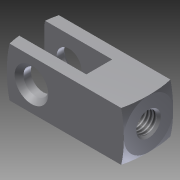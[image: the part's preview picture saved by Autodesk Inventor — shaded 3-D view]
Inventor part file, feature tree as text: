
AUTODESK INVENTOR PART (.ipt)
format: ipt  version: 2012 (Build 160160000, 160)  size: 180,224 bytes
history: native  units: in
note: dims shown in document units (in); Inventor stores cm internally (conversion verified against a paired STEP export)
features: other x126, sketch x7, revolve x3, extrude x2, hole x2
ambient origin geometry x8: Origin, YZ Plane, XZ Plane, XY Plane, X Axis, Y Axis, Z Axis, Center Point
bodies: Solid1 (feature_tree)
feature tree (140):
  extrude  "Extrusion1"  Depth=0.5in TaperAngle=0.0deg
  extrude  "Extrusion2"  TaperAngle=360.0deg  [1 undecoded]
  hole  "Drilling 1"  [1 undecoded]
  hole  "Drilling 2"  [1 undecoded]
  revolve  "Revolution1"  [1 undecoded]
  revolve  "Revolution2"  [1 undecoded]
  revolve  "Revolution3"  [1 undecoded]
  other  "th1_XY"
  other  "th1_YZ"
  other  "th1_ZX"
  other  "th1_X"
  other  "th1_Y"
  other  "th1_Z"
  other  "th1_Center"
  other  "th2_XY"
  other  "th2_YZ"
  other  "th2_ZX"
  other  "th2_X"
  other  "th2_Y"
  other  "th2_Z"
  other  "th2_Center"
  other  "rod_clevis_body_XY"
  other  "rod_clevis_body_YZ"
  other  "rod_clevis_body_ZX"
  other  "rod_clevis_body_X"
  other  "rod_clevis_body_Y"
  other  "rod_clevis_body_Z"
  other  "rod_clevis_body_Center"
  other  "piston_rod_clevis_XY"
  other  "piston_rod_clevis_YZ"
  other  "piston_rod_clevis_ZX"
  other  "piston_rod_clevis_X"
  other  "piston_rod_clevis_Y"
  other  "piston_rod_clevis_Z"
  other  "piston_rod_clevis_Center"
  other  "dummy_XY"
  other  "dummy_YZ"
  other  "dummy_ZX"
  other  "dummy_X"
  other  "dummy_Y"
  other  "dummy_Z"
  other  "dummy_Center"
  other  "l11_XY"
  other  "l11_YZ"
  other  "l11_ZX"
  other  "l11_X"
  other  "l11_Y"
  other  "l11_Z"
  other  "l11_Center"
  other  "l12_XY"
  other  "l12_YZ"
  other  "l12_ZX"
  other  "l12_X"
  other  "l12_Y"
  other  "l12_Z"
  other  "l12_Center"
  other  "l1_XY"
  other  "l1_YZ"
  other  "l1_ZX"
  other  "l1_X"
  other  "l1_Y"
  other  "l1_Z"
  other  "l1_Center"
  other  "h1_XY"
  other  "h1_YZ"
  other  "h1_ZX"
  other  "h1_X"
  other  "h1_Y"
  other  "h1_Z"
  other  "h1_Center"
  other  "l2_XY"
  other  "l2_YZ"
  other  "l2_ZX"
  other  "l2_X"
  other  "l2_Y"
  other  "l2_Z"
  other  "l2_Center"
  other  "h2_XY"
  other  "h2_YZ"
  other  "h2_ZX"
  other  "h2_X"
  other  "h2_Y"
  other  "h2_Z"
  other  "h2_Center"
  other  "w11_XY"
  other  "w11_YZ"
  other  "w11_ZX"
  other  "w11_X"
  other  "w11_Y"
  other  "w11_Z"
  other  "w11_Center"
  other  "w12_XY"
  other  "w12_YZ"
  other  "w12_ZX"
  other  "w12_X"
  other  "w12_Y"
  other  "w12_Z"
  other  "w12_Center"
  other  "l21_XY"
  other  "l21_YZ"
  other  "l21_ZX"
  other  "l21_X"
  other  "l21_Y"
  other  "l21_Z"
  other  "l21_Center"
  other  "l22_XY"
  other  "l22_YZ"
  other  "l22_ZX"
  other  "l22_X"
  other  "l22_Y"
  other  "l22_Z"
  other  "l22_Center"
  other  "w1_XY"
  other  "w1_YZ"
  other  "w1_ZX"
  other  "w1_X"
  other  "w1_Y"
  other  "w1_Z"
  other  "w1_Center"
  other  "w2_XY"
  other  "w2_YZ"
  other  "w2_ZX"
  other  "w2_X"
  other  "w2_Y"
  other  "w2_Z"
  other  "w2_Center"
  other  "to_cylinder_XY"
  other  "to_cylinder_YZ"
  other  "to_cylinder_ZX"
  other  "to_cylinder_X"
  other  "to_cylinder_Y"
  other  "to_cylinder_Z"
  other  "to_cylinder_Center"
  sketch  "Sketch_1"  dims[d0=0.5in d1=0.0in d2=0.5in d3=0.0in]
  sketch  "Sketch_2"  dims[d4=0.211in d5=0.44in d6=0.25in d7=0.25in d8=90.0deg d9=0.44in d10=0.0in]
  sketch  "Sketch3"  dims[d11=0.213in d12=0.75in d13=0.375in d14=0.25in d15=0.5635in d16=0.06in d17=0.0in d18=360.0deg]
  sketch  "Sketch4"  dims[d19=360.0deg d20=360.0deg]
  sketch  "Sketch_5"
  sketch  "Sketch_9"
  sketch  "Sketch_10"
note: 6 required parameter values undecoded (feature->parameter linkage not recoverable at this tier; creation-order binding heuristic only, values carry confidence <= 0.55)
